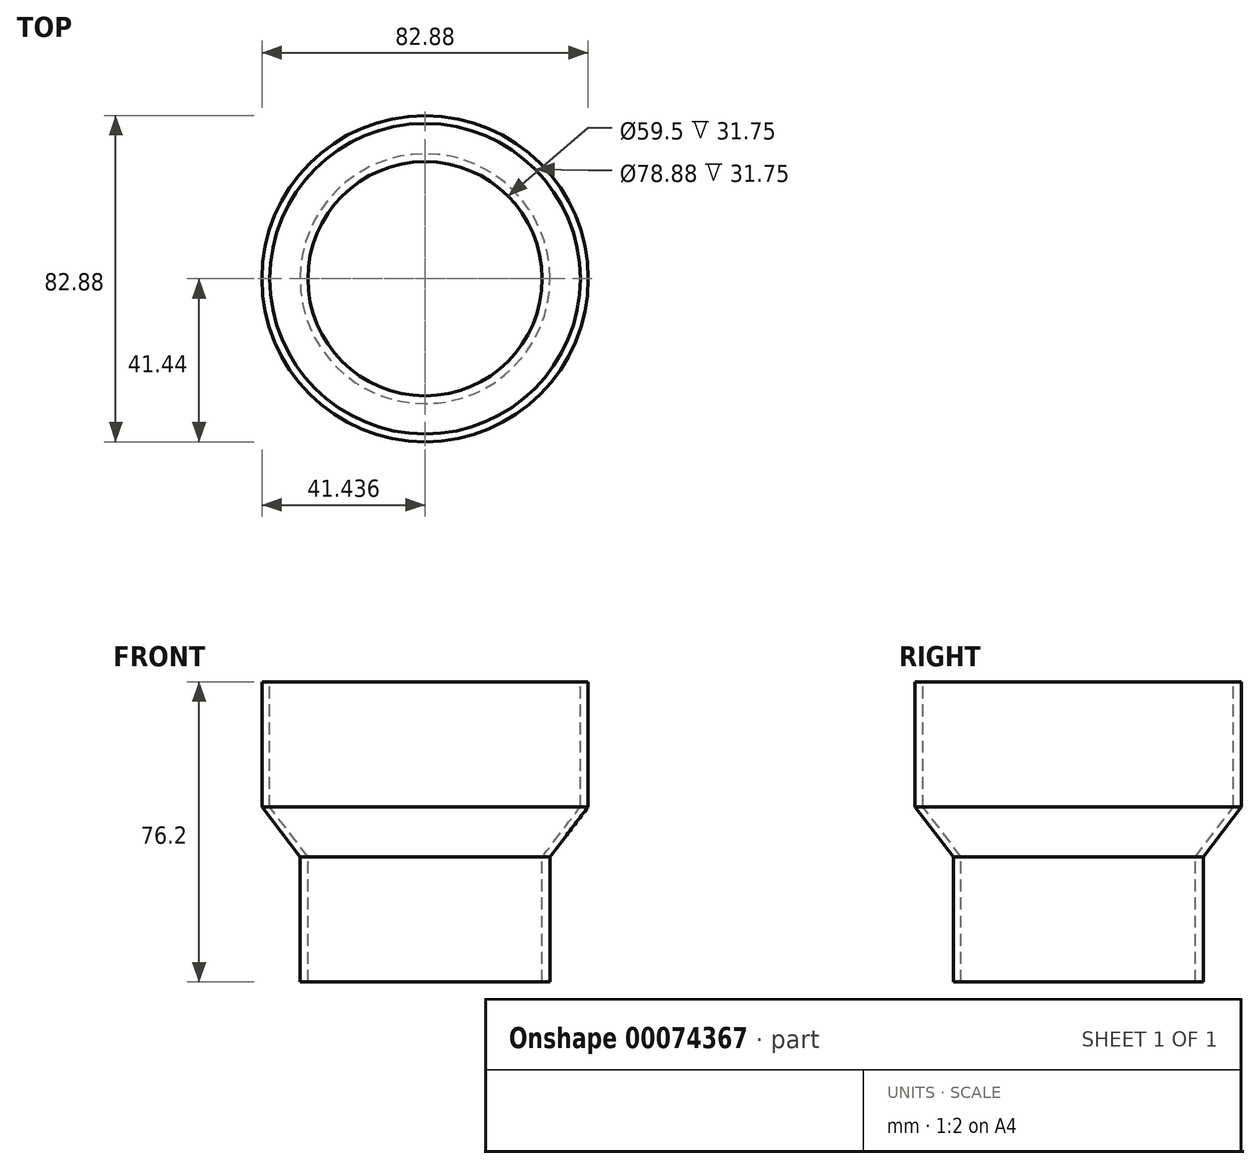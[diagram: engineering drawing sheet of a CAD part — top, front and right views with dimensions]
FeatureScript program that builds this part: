
annotation { "Feature Type Name" : "Feature", "Feature Type Description" : "" }
export const myFeature = defineFeature(function(context is Context, id is Id, definition is map)
    precondition{}
    {
        {
            var Q0;
            Q0=qCreatedBy(makeId("Front.planeOp"),FACE);
            var sketch = newSketch(context, id + "F0", { "sketchPlane" : qUnion([Q0])});
            skLineSegment(sketch, "E0.bottom", {"start": v(23.92, 31.75) * mm, "end": v(25.92, 31.75) * mm});
            skLineSegment(sketch, "E0.top", {"start": v(23.92, 0) * mm, "end": v(25.92, 0) * mm});
            skLineSegment(sketch, "E0.left", {"start": v(23.92, 31.75) * mm, "end": v(23.92, 0) * mm});
            skLineSegment(sketch, "E0.right", {"start": v(25.92, 31.75) * mm, "end": v(25.92, 0) * mm});
            skLineSegment(sketch, "E1.bottom", {"start": v(33.6, 76.2) * mm, "end": v(35.6, 76.2) * mm});
            skLineSegment(sketch, "E1.top", {"start": v(33.6, 44.45) * mm, "end": v(35.6, 44.45) * mm});
            skLineSegment(sketch, "E1.left", {"start": v(33.6, 76.2) * mm, "end": v(33.6, 44.45) * mm});
            skLineSegment(sketch, "E1.right", {"start": v(35.6, 76.2) * mm, "end": v(35.6, 44.45) * mm});
            skLineSegment(sketch, "E2", {"start": v(23.92, 31.75) * mm, "end": v(33.6, 44.45) * mm});
            skLineSegment(sketch, "E3", {"start": v(25.92, 31.75) * mm, "end": v(35.6, 44.45) * mm});
            skLineSegment(sketch, "E4", {"start": v(-5.83, 30.65) * mm, "end": v(-5.83, -26.8) * mm, "construction": true});
            skLineSegment(sketch, "E5", {"start": v(23.92, 0) * mm, "end": v(23.92, 31.75) * mm});
            skLineSegment(sketch, "E6", {"start": v(23.92, 31.75) * mm, "end": v(23.92, 31.75) * mm});
            skSolve(sketch);
        }
        {
            var Q0;
            Q0=makeQuery(id+"F0.imprint","IMPRINT",FACE,{"disambiguationData":[TD([[makeQuery(id+"F0.imprint","IMPRINT",EDGE,{"derivedFrom":sQuery(id+"F0.wireOp",EDGE,"E0.bottom")}),1.0]])]});
            var Q1;
            Q1=makeQuery(id+"F0.imprint","IMPRINT",FACE,{"disambiguationData":[TD([[makeQuery(id+"F0.imprint","IMPRINT",EDGE,{"derivedFrom":sQuery(id+"F0.wireOp",EDGE,"E1.bottom")}),-1.0]])]});
            var Q2;
            Q2=makeQuery(id+"F0.imprint","IMPRINT",FACE,{"disambiguationData":[TD([[makeQuery(id+"F0.imprint","IMPRINT",EDGE,{"derivedFrom":sQuery(id+"F0.wireOp",EDGE,"E0.bottom")}),-1.0]])]});
            var Q3;
            Q3=sQuery(id+"F0.wireOp",EDGE,"E4");
            revolve(context, id + "F1", {"surfaceOperationType" : NewSurfaceOperationType.NEW, "entities" : qUnion([Q0, Q1, Q2]), "axis" : qUnion([Q3]), "revolveType" : RevolveType.FULL});
        }
    });
